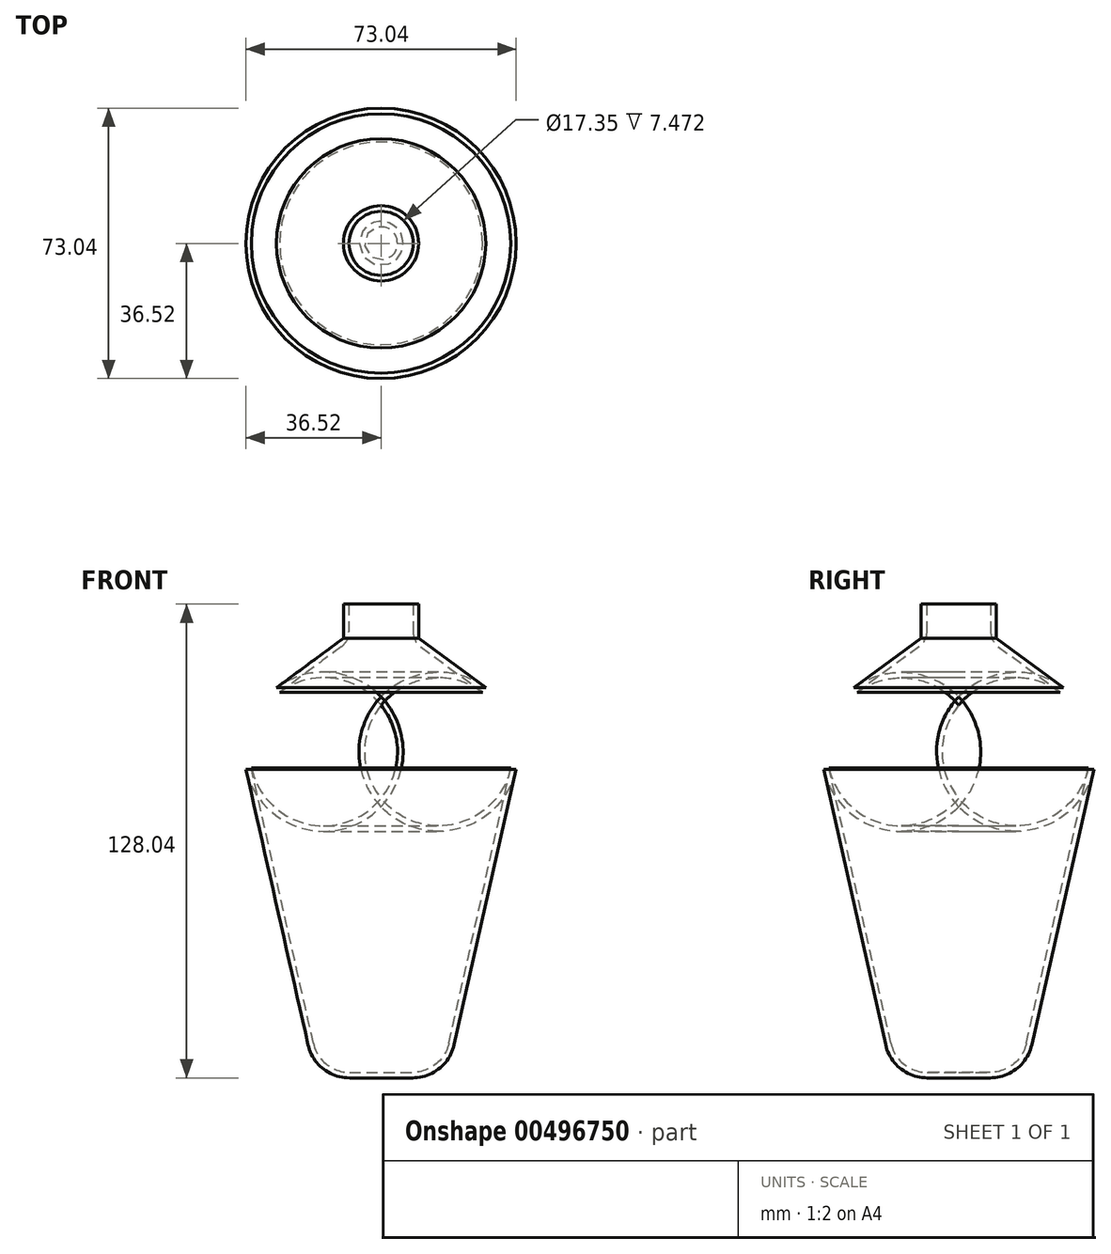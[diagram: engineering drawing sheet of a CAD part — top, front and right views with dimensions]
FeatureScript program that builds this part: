
annotation { "Feature Type Name" : "Feature", "Feature Type Description" : "" }
export const myFeature = defineFeature(function(context is Context, id is Id, definition is map)
    precondition{}
    {
        {
            var Q0;
            Q0=qCreatedBy(makeId("Front.planeOp"),FACE);
            var sketch = newSketch(context, id + "F0", { "sketchPlane" : qUnion([Q0])});
            skLineSegment(sketch, "E0", {"start": v(-8.67, 72.38) * mm, "end": v(-8.67, 64.9) * mm});
            skLineSegment(sketch, "E1", {"start": v(-10.7, 60.88) * mm, "end": v(-27.4, 48.6) * mm});
            skLineSegment(sketch, "E2", {"start": v(-35.05, 28.1) * mm, "end": v(-18.29, -46.36) * mm});
            skLineSegment(sketch, "E3", {"start": v(-8.53, -54.16) * mm, "end": v(0, -54.16) * mm});
            skPoint(sketch, "E4.visualSharp", {"position": v(-37.93, 40.84) * mm});
            skArc(sketch, "E4.filletArc", {"start": v(-27.4, 48.6) * mm, "mid": v(-34.28, 39.48) * mm, "end": v(-35.05, 28.1) * mm});
            skPoint(sketch, "E5.visualSharp", {"position": v(-16.53, -54.16) * mm});
            skArc(sketch, "E5.filletArc", {"start": v(-18.29, -46.36) * mm, "mid": v(-14.78, -51.97) * mm, "end": v(-8.53, -54.16) * mm});
            skPoint(sketch, "E6.visualSharp", {"position": v(-8.67, 62.38) * mm});
            skArc(sketch, "E6.filletArc", {"start": v(-10.7, 60.88) * mm, "mid": v(-9.21, 62.65) * mm, "end": v(-8.67, 64.9) * mm});
            skArc(sketch, "E7.0", {"start": v(-19.75, -46.69) * mm, "mid": v(-15.71, -53.14) * mm, "end": v(-8.53, -55.66) * mm});
            skLineSegment(sketch, "E7.1", {"start": v(-10.17, 72.38) * mm, "end": v(-10.17, 63.14) * mm});
            skLineSegment(sketch, "E7.2", {"start": v(-10.17, 63.14) * mm, "end": v(-28.29, 49.8) * mm});
            skArc(sketch, "E7.3", {"start": v(-28.29, 49.8) * mm, "mid": v(-35.68, 40) * mm, "end": v(-36.52, 27.76) * mm});
            skLineSegment(sketch, "E7.4", {"start": v(-36.52, 27.76) * mm, "end": v(-19.75, -46.69) * mm});
            skLineSegment(sketch, "E8", {"start": v(-8.53, -55.66) * mm, "end": v(0, -55.66) * mm});
            skLineSegment(sketch, "E9", {"start": v(0, -55.66) * mm, "end": v(0, -54.16) * mm});
            skLineSegment(sketch, "E10", {"start": v(-10.17, 72.38) * mm, "end": v(-8.67, 72.38) * mm});
            skSolve(sketch);
        }
        {
            var Q0;
            Q0 = qSketchRegion(id + "F0", true);
            var Q1;
            Q1=sQuery(id+"F0.wireOp",EDGE,"E9");
            revolve(context, id + "F1", {"entities" : qUnion([Q0]), "axis" : qUnion([Q1]), "revolveType" : RevolveType.FULL});
        }
    });
